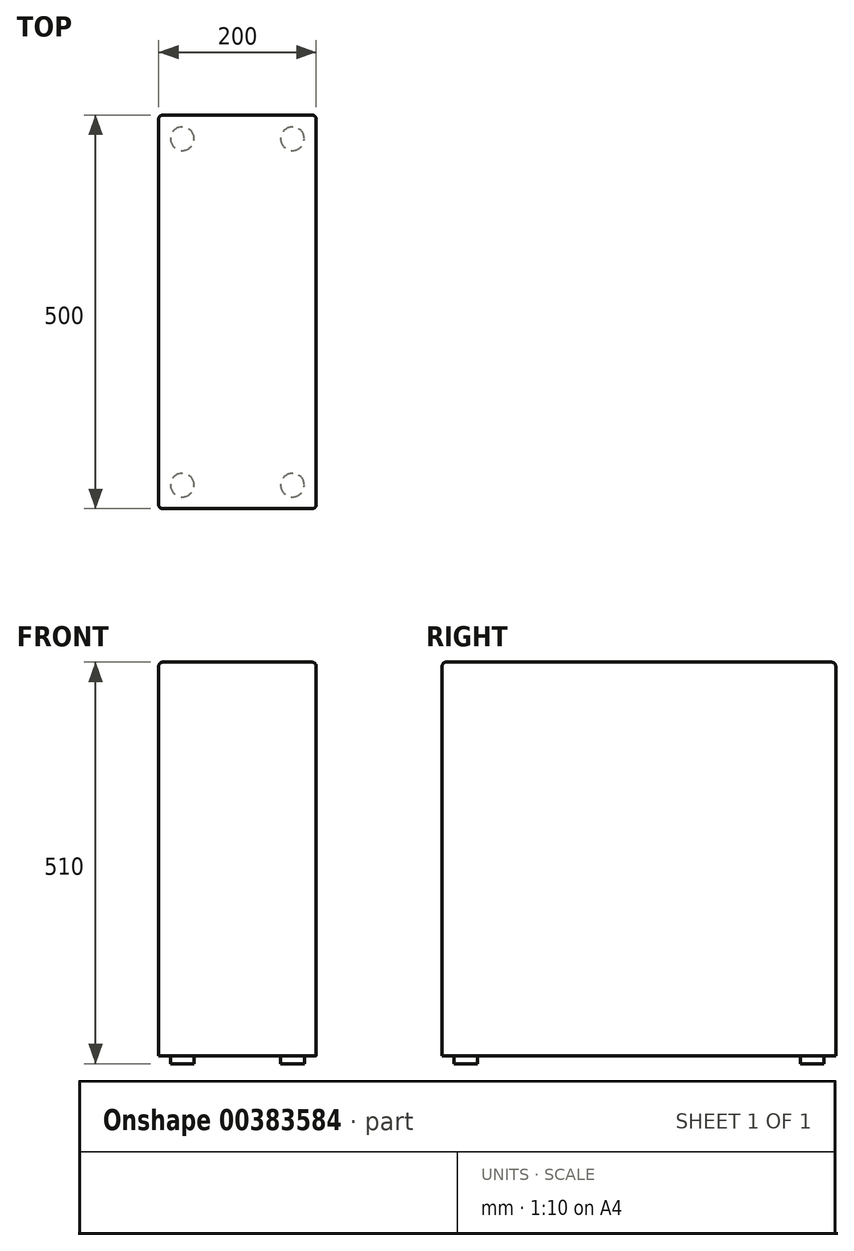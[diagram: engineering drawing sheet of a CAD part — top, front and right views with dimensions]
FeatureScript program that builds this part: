
annotation { "Feature Type Name" : "Feature", "Feature Type Description" : "" }
export const myFeature = defineFeature(function(context is Context, id is Id, definition is map)
    precondition{}
    {
        {
            var Q0;
            Q0=qCreatedBy(makeId("Top.planeOp"),FACE);
            var sketch = newSketch(context, id + "F0", { "sketchPlane" : qUnion([Q0])});
            skLineSegment(sketch, "E0.bottom", {"start": v(100, -250) * mm, "end": v(-100, -250) * mm});
            skLineSegment(sketch, "E0.top", {"start": v(100, 250) * mm, "end": v(-100, 250) * mm});
            skLineSegment(sketch, "E0.left", {"start": v(100, -250) * mm, "end": v(100, 250) * mm});
            skLineSegment(sketch, "E0.right", {"start": v(-100, -250) * mm, "end": v(-100, 250) * mm});
            skPoint(sketch, "E0.middle", {"position": v(0, 0) * mm});
            skSolve(sketch);
        }
        {
            var Q0;
            Q0=makeQuery(id+"F0.imprint","IMPRINT",FACE,{"disambiguationData":[TD([[makeQuery(id+"F0.imprint","IMPRINT",EDGE,{"derivedFrom":sQuery(id+"F0.wireOp",EDGE,"E0.bottom")}),-1.0]])]});
            extrude(context, id + "F1", {"entities" : qUnion([Q0]), "depth" : 500 * mm});
        }
        {
            var Q0;
            Q0=makeQuery(id+"F1.opExtrude","CAP_FACE",FACE,{"disambiguationData":[OSD([sQuery(id+"F0.wireOp",EDGE,"E0.bottom"),sQuery(id+"F0.wireOp",EDGE,"E0.top"),sQuery(id+"F0.wireOp",EDGE,"E0.left"),sQuery(id+"F0.wireOp",EDGE,"E0.right")])],"isStart":true});
            var sketch = newSketch(context, id + "F2", { "sketchPlane" : qUnion([Q0])});
            skCircle(sketch, "E1", {"center": v(-70, 220) * mm, "radius": 15 * mm});
            skCircle(sketch, "E2.0.1.0", {"center": v(-70, -220) * mm, "radius": 15 * mm});
            skCircle(sketch, "E2.1.0.0", {"center": v(70, 220) * mm, "radius": 15 * mm});
            skCircle(sketch, "E2.1.1.0", {"center": v(70, -220) * mm, "radius": 15 * mm});
            skLineSegment(sketch, "E2.direction1", {"start": v(-70, 220) * mm, "end": v(70, 220) * mm, "construction": true});
            skLineSegment(sketch, "E2.direction2", {"start": v(-70, 220) * mm, "end": v(-70, -220) * mm, "construction": true});
            skSolve(sketch);
        }
        {
            var Q0;
            Q0=makeQuery(id+"F2.imprint","IMPRINT",FACE,{"disambiguationData":[TD([[makeQuery(id+"F2.imprint","IMPRINT",EDGE,{"derivedFrom":sQuery(id+"F2.wireOp",EDGE,"E1")}),1.0]])]});
            var Q1;
            Q1=makeQuery(id+"F2.imprint","IMPRINT",FACE,{"disambiguationData":[TD([[makeQuery(id+"F2.imprint","IMPRINT",EDGE,{"derivedFrom":sQuery(id+"F2.wireOp",EDGE,"E2.1.0.0")}),1.0]])]});
            var Q2;
            Q2=makeQuery(id+"F2.imprint","IMPRINT",FACE,{"disambiguationData":[TD([[makeQuery(id+"F2.imprint","IMPRINT",EDGE,{"derivedFrom":sQuery(id+"F2.wireOp",EDGE,"E2.0.1.0")}),1.0]])]});
            var Q3;
            Q3=makeQuery(id+"F2.imprint","IMPRINT",FACE,{"disambiguationData":[TD([[makeQuery(id+"F2.imprint","IMPRINT",EDGE,{"derivedFrom":sQuery(id+"F2.wireOp",EDGE,"E2.1.1.0")}),1.0]])]});
            extrude(context, id + "F3", {"entities" : qUnion([Q0, Q1, Q2, Q3]), "depth" : 10 * mm});
        }
        {
            var Q0;
            Q0=makeQuery(id+"F1.opExtrude","CAP_EDGE",EDGE,{"disambiguationData":[OSD([sQuery(id+"F0.wireOp",EDGE,"E0.right")])],"isStart":false});
            var Q1;
            Q1=makeQuery(id+"F1.opExtrude","SWEPT_EDGE",EDGE,{"disambiguationData":[OSD([sQuery(id+"F0.wireOp",EDGE,"E0.bottom"),sQuery(id+"F0.wireOp",EDGE,"E0.right")])]});
            var Q2;
            Q2=makeQuery(id+"F1.opExtrude","SWEPT_EDGE",EDGE,{"disambiguationData":[OSD([sQuery(id+"F0.wireOp",EDGE,"E0.top"),sQuery(id+"F0.wireOp",EDGE,"E0.right")])]});
            var Q3;
            Q3=makeQuery(id+"F1.opExtrude","CAP_EDGE",EDGE,{"disambiguationData":[OSD([sQuery(id+"F0.wireOp",EDGE,"E0.top")])],"isStart":false});
            var Q4;
            Q4=makeQuery(id+"F1.opExtrude","CAP_EDGE",EDGE,{"disambiguationData":[OSD([sQuery(id+"F0.wireOp",EDGE,"E0.left")])],"isStart":false});
            var Q5;
            Q5=makeQuery(id+"F1.opExtrude","CAP_EDGE",EDGE,{"disambiguationData":[OSD([sQuery(id+"F0.wireOp",EDGE,"E0.bottom")])],"isStart":false});
            var Q6;
            Q6=makeQuery(id+"F1.opExtrude","SWEPT_EDGE",EDGE,{"disambiguationData":[OSD([sQuery(id+"F0.wireOp",EDGE,"E0.bottom"),sQuery(id+"F0.wireOp",EDGE,"E0.left")])]});
            var Q7;
            Q7=makeQuery(id+"F1.opExtrude","SWEPT_EDGE",EDGE,{"disambiguationData":[OSD([sQuery(id+"F0.wireOp",EDGE,"E0.top"),sQuery(id+"F0.wireOp",EDGE,"E0.left")])]});
            fillet(context, id + "F4", {"entities" : qUnion([Q0, Q1, Q2, Q3, Q4, Q5, Q6, Q7]), "radius" : 5 * mm, "tangentPropagation" : true, "allowEdgeOverflow" : false});
        }
    });
